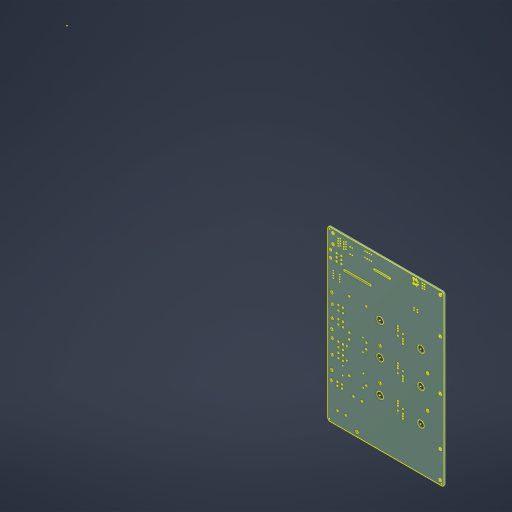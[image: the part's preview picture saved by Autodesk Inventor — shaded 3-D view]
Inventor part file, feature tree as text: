
AUTODESK INVENTOR PART (.ipt)
format: ipt  version: 2024.2 (Build 282272000, 272)  size: 426,496 bytes
history: native  units: in
note: dims shown in document units (in); Inventor stores cm internally (conversion verified against a paired STEP export)
features: sketch x1, projected_geometry x1, imported_body x1
ambient origin geometry x8: Origin, YZ Plane, XZ Plane, XY Plane, X Axis, Y Axis, Z Axis, Center Point
bodies: Solid1 (feature_tree)
feature tree (3):
  sketch  "Sketch1"
  projected_geometry  "Projected Loop1"
  imported_body  "Base1"
